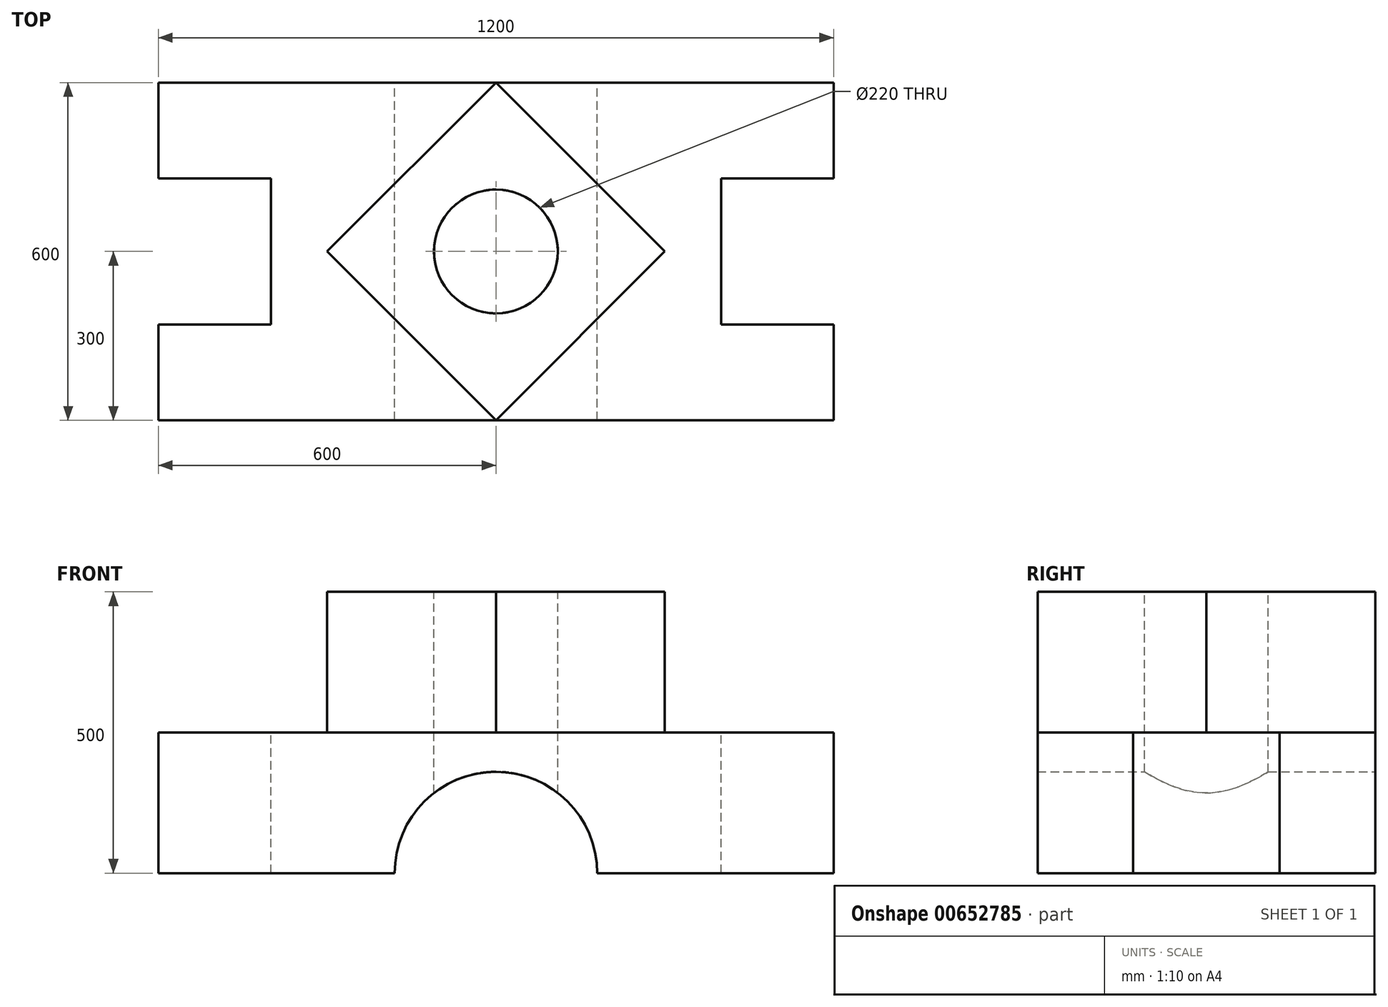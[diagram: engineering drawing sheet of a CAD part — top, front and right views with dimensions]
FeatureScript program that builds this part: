
annotation { "Feature Type Name" : "Feature", "Feature Type Description" : "" }
export const myFeature = defineFeature(function(context is Context, id is Id, definition is map)
    precondition{}
    {
        {
            var Q0;
            Q0=qCreatedBy(makeId("Front.planeOp"),FACE);
            var sketch = newSketch(context, id + "F0", { "sketchPlane" : qUnion([Q0])});
            skLineSegment(sketch, "E0.bottom", {"start": v(-600, -125) * mm, "end": v(-180, -125) * mm});
            skLineSegment(sketch, "E0.top", {"start": v(-600, 125) * mm, "end": v(-300, 125) * mm});
            skLineSegment(sketch, "E0.left", {"start": v(-600, -125) * mm, "end": v(-600, 125) * mm});
            skLineSegment(sketch, "E0.right", {"start": v(600, -125) * mm, "end": v(600, 125) * mm});
            skPoint(sketch, "E0.middle", {"position": v(0, 0) * mm});
            skLineSegment(sketch, "E1.top", {"start": v(-300, 375) * mm, "end": v(300, 375) * mm});
            skLineSegment(sketch, "E1.left", {"start": v(-300, 125) * mm, "end": v(-300, 375) * mm});
            skLineSegment(sketch, "E1.right", {"start": v(300, 125) * mm, "end": v(300, 375) * mm});
            skPoint(sketch, "E1.middle", {"position": v(0, 125) * mm});
            skArc(sketch, "E2", {"start": v(180, -125) * mm, "mid": v(0, 55) * mm, "end": v(-180, -125) * mm});
            skPoint(sketch, "E3.orphan", {"position": v(-300, -125) * mm});
            skLineSegment(sketch, "E4.trimOffspring", {"start": v(300, 125) * mm, "end": v(600, 125) * mm});
            skPoint(sketch, "E5.orphan", {"position": v(300, -125) * mm});
            skLineSegment(sketch, "E6.trimOffspring", {"start": v(180, -125) * mm, "end": v(600, -125) * mm});
            skSolve(sketch);
        }
        {
            var Q0;
            Q0 = qSketchRegion(id + "F0", true);
            extrude(context, id + "F1", {"entities" : qUnion([Q0]), "depth" : 600 * mm, "offsetDistance" : 25 * mm});
        }
        {
            var Q0;
            Q0=makeQuery(id+"F1.opExtrude","SWEPT_FACE",FACE,{"disambiguationData":[OSD([sQuery(id+"F0.wireOp",EDGE,"E0.top")])]});
            var sketch = newSketch(context, id + "F2", { "sketchPlane" : qUnion([Q0])});
            skLineSegment(sketch, "E7.bottom", {"start": v(-400, -430) * mm, "end": v(-800, -430) * mm});
            skLineSegment(sketch, "E7.top", {"start": v(-400, -170) * mm, "end": v(-800, -170) * mm});
            skLineSegment(sketch, "E7.left", {"start": v(-400, -430) * mm, "end": v(-400, -170) * mm});
            skLineSegment(sketch, "E7.right", {"start": v(-800, -430) * mm, "end": v(-800, -170) * mm});
            skPoint(sketch, "E7.middle", {"position": v(-600, -300) * mm});
            skSolve(sketch);
        }
        {
            var Q0;
            Q0 = qSketchRegion(id + "F2", true);
            extrude(context, id + "F3", {"entities" : qUnion([Q0]), "operationType" : NewBodyOperationType.REMOVE, "endBound" : BoundingType.THROUGH_ALL, "oppositeDirection" : true, "depth" : 25 * mm, "offsetDistance" : 25 * mm});
        }
        {
            var Q0;
            Q0=makeQuery(id+"F1.opExtrude","SWEPT_FACE",FACE,{"disambiguationData":[OSD([sQuery(id+"F0.wireOp",EDGE,"E4.trimOffspring")])]});
            var sketch = newSketch(context, id + "F4", { "sketchPlane" : qUnion([Q0])});
            skLineSegment(sketch, "E8.bottom", {"start": v(400, -430) * mm, "end": v(800, -430) * mm});
            skLineSegment(sketch, "E8.top", {"start": v(400, -170) * mm, "end": v(800, -170) * mm});
            skLineSegment(sketch, "E8.left", {"start": v(400, -430) * mm, "end": v(400, -170) * mm});
            skLineSegment(sketch, "E8.right", {"start": v(800, -430) * mm, "end": v(800, -170) * mm});
            skPoint(sketch, "E8.middle", {"position": v(600, -300) * mm});
            skSolve(sketch);
        }
        {
            var Q0;
            Q0 = qSketchRegion(id + "F4", true);
            extrude(context, id + "F5", {"entities" : qUnion([Q0]), "operationType" : NewBodyOperationType.REMOVE, "endBound" : BoundingType.THROUGH_ALL, "oppositeDirection" : true, "depth" : 25 * mm, "offsetDistance" : 25 * mm});
        }
        {
            var Q0;
            Q0=makeQuery(id+"F1.opExtrude","SWEPT_FACE",FACE,{"disambiguationData":[OSD([sQuery(id+"F0.wireOp",EDGE,"E1.top")])]});
            var sketch = newSketch(context, id + "F6", { "sketchPlane" : qUnion([Q0])});
            skLineSegment(sketch, "E9", {"start": v(300, -300) * mm, "end": v(0, -600) * mm});
            skLineSegment(sketch, "E10", {"start": v(0, -600) * mm, "end": v(-300, -300) * mm});
            skLineSegment(sketch, "E11", {"start": v(-300, -300) * mm, "end": v(0, 0) * mm});
            skLineSegment(sketch, "E12", {"start": v(0, 0) * mm, "end": v(-300, 0) * mm});
            skLineSegment(sketch, "E13", {"start": v(-300, 0) * mm, "end": v(-300, -600) * mm});
            skLineSegment(sketch, "E14", {"start": v(-300, -600) * mm, "end": v(300, -600) * mm});
            skLineSegment(sketch, "E15", {"start": v(300, -600) * mm, "end": v(300, -300) * mm});
            skSolve(sketch);
        }
        {
            var Q0;
            Q0 = qSketchRegion(id + "F6", true);
            extrude(context, id + "F7", {"entities" : qUnion([Q0]), "operationType" : NewBodyOperationType.REMOVE, "oppositeDirection" : true, "depth" : 250 * mm, "offsetDistance" : 25 * mm});
        }
        {
            var Q0;
            Q0=makeQuery(id+"F1.opExtrude","SWEPT_FACE",FACE,{"disambiguationData":[OSD([sQuery(id+"F0.wireOp",EDGE,"E1.top")])]});
            var sketch = newSketch(context, id + "F8", { "sketchPlane" : qUnion([Q0])});
            skLineSegment(sketch, "E16", {"start": v(0, 0) * mm, "end": v(300, -300) * mm});
            skLineSegment(sketch, "E17", {"start": v(300, -300) * mm, "end": v(300, 0) * mm});
            skLineSegment(sketch, "E18", {"start": v(300, 0) * mm, "end": v(0, 0) * mm});
            skSolve(sketch);
        }
        {
            var Q0;
            Q0 = qSketchRegion(id + "F8", true);
            extrude(context, id + "F9", {"entities" : qUnion([Q0]), "operationType" : NewBodyOperationType.REMOVE, "oppositeDirection" : true, "depth" : 250 * mm, "offsetDistance" : 25 * mm});
        }
        {
            var Q0;
            Q0=makeQuery(id+"F1.opExtrude","SWEPT_FACE",FACE,{"disambiguationData":[OSD([sQuery(id+"F0.wireOp",EDGE,"E1.top")])]});
            var sketch = newSketch(context, id + "F10", { "sketchPlane" : qUnion([Q0])});
            skCircle(sketch, "E19", {"center": v(0, -300) * mm, "radius": 110 * mm});
            skSolve(sketch);
        }
        {
            var Q0;
            Q0 = qSketchRegion(id + "F10", true);
            extrude(context, id + "F11", {"entities" : qUnion([Q0]), "operationType" : NewBodyOperationType.REMOVE, "endBound" : BoundingType.THROUGH_ALL, "oppositeDirection" : true, "depth" : 25 * mm, "offsetDistance" : 25 * mm});
        }
    });
